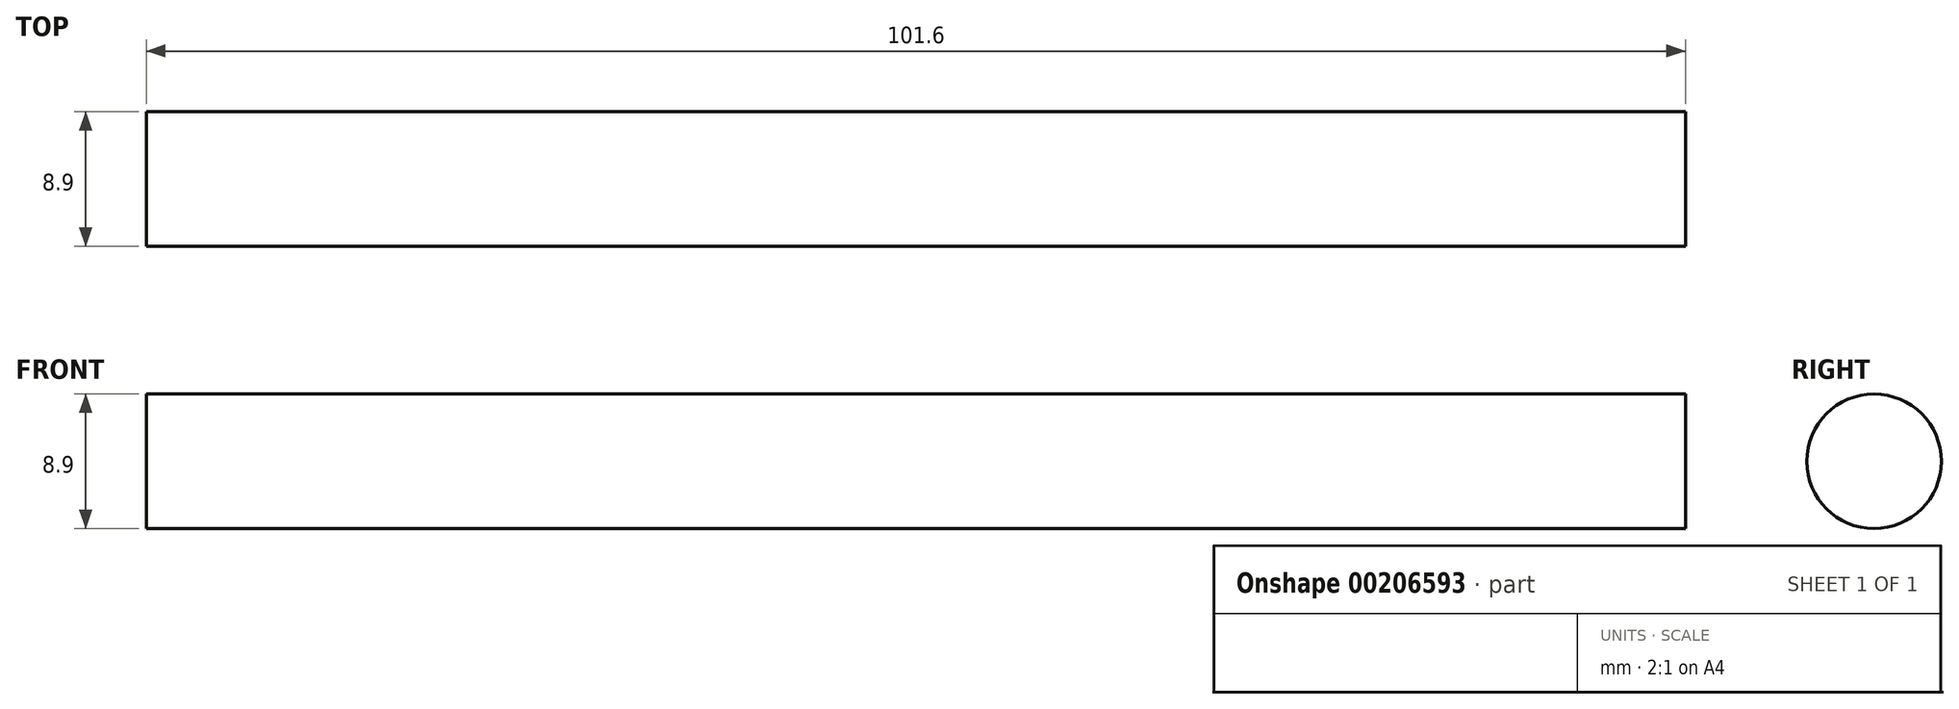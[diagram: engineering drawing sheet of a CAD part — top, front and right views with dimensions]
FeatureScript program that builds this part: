
annotation { "Feature Type Name" : "Feature", "Feature Type Description" : "" }
export const myFeature = defineFeature(function(context is Context, id is Id, definition is map)
    precondition{}
    {
        {
            var Q0;
            Q0=qCreatedBy(makeId("Right.planeOp"),FACE);
            var sketch = newSketch(context, id + "F0", { "sketchPlane" : qUnion([Q0])});
            skCircle(sketch, "E0", {"center": v(0, 0) * mm, "radius": 4.45 * mm});
            skSolve(sketch);
        }
        {
            var Q0;
            Q0=makeQuery(id+"F0.imprint","IMPRINT",FACE,{"disambiguationData":[TD([[makeQuery(id+"F0.imprint","IMPRINT",EDGE,{"derivedFrom":sQuery(id+"F0.wireOp",EDGE,"E0")}),1.0]])]});
            var Q1;
            Q1=sQuery(id+"F0.wireOp",EDGE,"E0");
            extrude(context, id + "F1", {"entities" : qUnion([Q0]), "surfaceEntities" : qUnion([Q1]), "depth" : 101.6 * mm});
        }
    });
